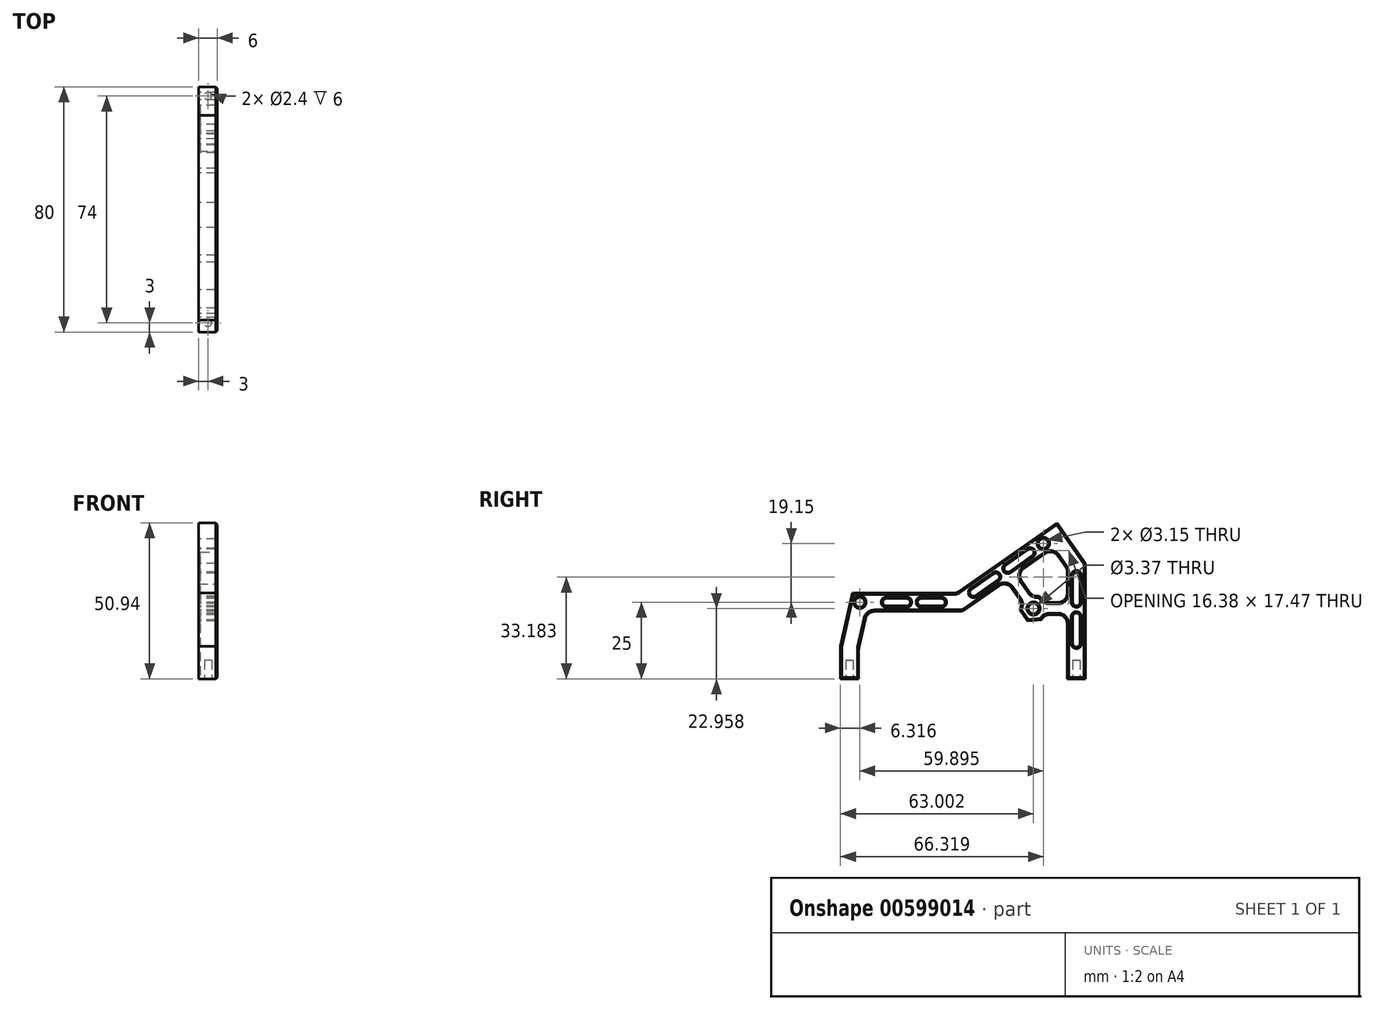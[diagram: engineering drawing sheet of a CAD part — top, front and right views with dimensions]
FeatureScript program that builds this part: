
annotation { "Feature Type Name" : "Feature", "Feature Type Description" : "" }
export const myFeature = defineFeature(function(context is Context, id is Id, definition is map)
    precondition{}
    {
        {
            var Q0;
            Q0=qCreatedBy(makeId("Top.planeOp"),FACE);
            var sketch = newSketch(context, id + "F0", { "sketchPlane" : qUnion([Q0])});
            skLineSegment(sketch, "E0", {"start": v(14, 40) * mm, "end": v(0, 40) * mm, "construction": true});
            skLineSegment(sketch, "E1", {"start": v(0, 40) * mm, "end": v(0, 0) * mm, "construction": true});
            skLineSegment(sketch, "E2", {"start": v(14, 40) * mm, "end": v(20, 40) * mm});
            skLineSegment(sketch, "E3", {"start": v(20, 40) * mm, "end": v(20, 0) * mm});
            skLineSegment(sketch, "E4", {"start": v(14, 40) * mm, "end": v(14, 0) * mm});
            skLineSegment(sketch, "E5.MirrorCS", {"start": v(14, -40) * mm, "end": v(20, -40) * mm});
            skLineSegment(sketch, "E6.MirrorCS", {"start": v(14, -40) * mm, "end": v(14, 0) * mm});
            skLineSegment(sketch, "E7.MirrorCS", {"start": v(20, -40) * mm, "end": v(20, 0) * mm});
            skLineSegment(sketch, "E8.MirrorCS", {"start": v(14, -40) * mm, "end": v(0, -40) * mm, "construction": true});
            skLineSegment(sketch, "E9.MirrorCS", {"start": v(0, -40) * mm, "end": v(0, 0) * mm, "construction": true});
            skLineSegment(sketch, "E10", {"start": v(14, 0) * mm, "end": v(29.88, 0) * mm, "construction": true});
            skLineSegment(sketch, "E11", {"start": v(20, 40) * mm, "end": v(20, 34) * mm, "construction": true});
            skPoint(sketch, "E12.centerSnap0", {"position": v(20, 37) * mm});
            skPoint(sketch, "E12.centerSnap1", {"position": v(17, 40) * mm});
            skSolve(sketch);
        }
        {
            var Q0;
            Q0=makeQuery(id+"F0.imprint","IMPRINT",FACE,{"disambiguationData":[TD([[makeQuery(id+"F0.imprint","IMPRINT",EDGE,{"derivedFrom":sQuery(id+"F0.wireOp",EDGE,"E2")}),-1.0]])]});
            extrude(context, id + "F1", {"entities" : qUnion([Q0]), "depth" : 70 * mm, "offsetDistance" : 25 * mm});
        }
        {
            var Q0;
            Q0=makeQuery(id+"F1.opExtrude","SWEPT_FACE",FACE,{"disambiguationData":[OSD([sQuery(id+"F0.wireOp",EDGE,"E4"),sQuery(id+"F0.wireOp",EDGE,"E6.MirrorCS")])]});
            var sketch = newSketch(context, id + "F2", { "sketchPlane" : qUnion([Q0])});
            skLineSegment(sketch, "E13", {"start": v(0, 0) * mm, "end": v(0, 28) * mm, "construction": true});
            skPoint(sketch, "E13.endSnap0", {"position": v(0, 0) * mm});
            skLineSegment(sketch, "E14", {"start": v(-20.33, 28) * mm, "end": v(19.67, 28) * mm, "construction": true});
            skLineSegment(sketch, "E15", {"start": v(2.08, 28) * mm, "end": v(-30.68, 50.94) * mm});
            skLineSegment(sketch, "E16", {"start": v(40, 10.6) * mm, "end": v(36.08, 28) * mm});
            skLineSegment(sketch, "E17", {"start": v(36.08, 28) * mm, "end": v(2.08, 28) * mm});
            skLineSegment(sketch, "E18", {"start": v(-30.68, 50.94) * mm, "end": v(-40, 37.64) * mm});
            skLineSegment(sketch, "E19", {"start": v(-40, 37.64) * mm, "end": v(-40, 0) * mm});
            skLineSegment(sketch, "E20", {"start": v(31.28, 22) * mm, "end": v(0.2, 22) * mm});
            skLineSegment(sketch, "E21", {"start": v(0.2, 22) * mm, "end": v(-14.18, 32.07) * mm});
            skLineSegment(sketch, "E22", {"start": v(-29.2, 42.59) * mm, "end": v(-34, 35.74) * mm});
            skLineSegment(sketch, "E23", {"start": v(-34, 35.74) * mm, "end": v(-34, 24.96) * mm});
            skLineSegment(sketch, "E24", {"start": v(-14.18, 32.07) * mm, "end": v(-21.96, 20.96) * mm});
            skLineSegment(sketch, "E25", {"start": v(-21.96, 20.96) * mm, "end": v(-34, 20.96) * mm});
            skLineSegment(sketch, "E26", {"start": v(-17.46, 34.36) * mm, "end": v(-24.04, 24.96) * mm});
            skLineSegment(sketch, "E27", {"start": v(-24.04, 24.96) * mm, "end": v(-34, 24.96) * mm});
            skLineSegment(sketch, "E28", {"start": v(-24.04, 24.96) * mm, "end": v(-21.96, 20.96) * mm, "construction": true});
            skCircle(sketch, "E29", {"center": v(-23, 22.96) * mm, "radius": 1.69 * mm});
            skLineSegment(sketch, "E30.trimOffspring", {"start": v(-17.46, 34.36) * mm, "end": v(-29.2, 42.59) * mm});
            skLineSegment(sketch, "E31.trimOffspring", {"start": v(-34, 20.96) * mm, "end": v(-34, 0) * mm});
            skLineSegment(sketch, "E32", {"start": v(-24.5, 46.6) * mm, "end": v(-26.21, 44.15) * mm, "construction": true});
            skCircle(sketch, "E33", {"center": v(-26.21, 44.15) * mm, "radius": 1.57 * mm});
            skLineSegment(sketch, "E34", {"start": v(36.08, 28) * mm, "end": v(31.28, 22) * mm, "construction": true});
            skCircle(sketch, "E35", {"center": v(33.68, 25) * mm, "radius": 1.57 * mm});
            skCircle(sketch, "E36.cCircle", {"center": v(-23, 22.96) * mm, "radius": 3.92 * mm, "construction": true});
            skLineSegment(sketch, "E36.0", {"start": v(-27.51, 23.35) * mm, "end": v(-24.92, 27.06) * mm});
            skLineSegment(sketch, "E36.1", {"start": v(-24.92, 27.06) * mm, "end": v(-20.4, 26.67) * mm});
            skLineSegment(sketch, "E36.2", {"start": v(-20.4, 26.67) * mm, "end": v(-18.5, 22.56) * mm});
            skLineSegment(sketch, "E36.3", {"start": v(-18.5, 22.56) * mm, "end": v(-21.09, 18.85) * mm});
            skLineSegment(sketch, "E36.4", {"start": v(-21.09, 18.85) * mm, "end": v(-25.6, 19.25) * mm});
            skLineSegment(sketch, "E36.5", {"start": v(-25.6, 19.25) * mm, "end": v(-27.51, 23.35) * mm});
            skPoint(sketch, "E36.0.midPoint", {"position": v(-26.21, 25.2) * mm});
            skLineSegment(sketch, "E37", {"start": v(-30.68, 50.94) * mm, "end": v(-30.68, 0) * mm, "construction": true});
            skLineSegment(sketch, "E38", {"start": v(-49.75, 0) * mm, "end": v(34, 0) * mm, "construction": true});
            skLineSegment(sketch, "E39", {"start": v(40, 10.6) * mm, "end": v(40, 0) * mm});
            skLineSegment(sketch, "E40", {"start": v(40, 0) * mm, "end": v(36.1, 0) * mm});
            skLineSegment(sketch, "E41", {"start": v(34, 9.92) * mm, "end": v(34, 0) * mm});
            skLineSegment(sketch, "E42.trimOffspring", {"start": v(42.25, 0) * mm, "end": v(49.74, 0) * mm, "construction": true});
            skLineSegment(sketch, "E43", {"start": v(40, 0) * mm, "end": v(34, 0) * mm});
            skLineSegment(sketch, "E44", {"start": v(31.28, 22) * mm, "end": v(34, 9.92) * mm});
            skLineSegment(sketch, "E45", {"start": v(0.2, 22) * mm, "end": v(31.28, 22) * mm});
            skLineSegment(sketch, "E46", {"start": v(40, 0) * mm, "end": v(40, 10.6) * mm});
            skLineSegment(sketch, "E47", {"start": v(7.02, 26.2) * mm, "end": v(13.64, 26.2) * mm});
            skLineSegment(sketch, "E48", {"start": v(2.08, 28) * mm, "end": v(2.08, 22) * mm, "construction": true});
            skLineSegment(sketch, "E49", {"start": v(7.02, 23.8) * mm, "end": v(7.02, 26.2) * mm, "construction": true});
            skLineSegment(sketch, "E50", {"start": v(25.02, 23.8) * mm, "end": v(25.02, 26.2) * mm, "construction": true});
            skCircle(sketch, "E51", {"center": v(7.02, 25) * mm, "radius": 1.2 * mm});
            skCircle(sketch, "E52", {"center": v(25.02, 25) * mm, "radius": 1.2 * mm});
            skLineSegment(sketch, "E53", {"start": v(-35.8, 33.72) * mm, "end": v(-35.8, 25.03) * mm});
            skLineSegment(sketch, "E54", {"start": v(-38.2, 33.72) * mm, "end": v(-38.2, 25.03) * mm});
            skLineSegment(sketch, "E55", {"start": v(-35.8, 33.72) * mm, "end": v(-38.2, 33.72) * mm, "construction": true});
            skLineSegment(sketch, "E56", {"start": v(-35.8, 11.57) * mm, "end": v(-38.2, 11.57) * mm, "construction": true});
            skCircle(sketch, "E57", {"center": v(-37, 33.72) * mm, "radius": 1.2 * mm});
            skCircle(sketch, "E58", {"center": v(-37, 11.57) * mm, "radius": 1.2 * mm});
            skLineSegment(sketch, "E59", {"start": v(-22.6, 40.16) * mm, "end": v(-15.28, 35.04) * mm});
            skLineSegment(sketch, "E60", {"start": v(-22.6, 40.16) * mm, "end": v(-21.23, 42.11) * mm, "construction": true});
            skLineSegment(sketch, "E61", {"start": v(-21.23, 42.11) * mm, "end": v(-13.92, 37) * mm});
            skLineSegment(sketch, "E62", {"start": v(-2.7, 29.14) * mm, "end": v(-4.07, 27.2) * mm, "construction": true});
            skCircle(sketch, "E63", {"center": v(-21.9, 41.14) * mm, "radius": 1.2 * mm});
            skCircle(sketch, "E64", {"center": v(-3.39, 28.17) * mm, "radius": 1.2 * mm});
            skLineSegment(sketch, "E65", {"start": v(5.46, 28) * mm, "end": v(5.46, 22) * mm, "construction": true});
            skLineSegment(sketch, "E66", {"start": v(5.46, 25) * mm, "end": v(7.02, 25) * mm, "construction": true});
            skLineSegment(sketch, "E67", {"start": v(-22.05, 44.9) * mm, "end": v(-25.5, 39.98) * mm, "construction": true});
            skLineSegment(sketch, "E68", {"start": v(-23.77, 42.44) * mm, "end": v(-21.9, 41.14) * mm, "construction": true});
            skLineSegment(sketch, "E69", {"start": v(-34, 35.47) * mm, "end": v(-40, 35.47) * mm, "construction": true});
            skLineSegment(sketch, "E70", {"start": v(-37, 35.47) * mm, "end": v(-37, 33.72) * mm, "construction": true});
            skLineSegment(sketch, "E71", {"start": v(16.02, 26.2) * mm, "end": v(16.02, 23.8) * mm, "construction": true});
            skLineSegment(sketch, "E72", {"start": v(-35.8, 22.65) * mm, "end": v(-38.2, 22.65) * mm, "construction": true});
            skLineSegment(sketch, "E73", {"start": v(-12.65, 34.65) * mm, "end": v(-21.9, 41.14) * mm, "construction": true});
            skLineSegment(sketch, "E74", {"start": v(-12.65, 34.65) * mm, "end": v(-3.39, 28.17) * mm, "construction": true});
            skLineSegment(sketch, "E75", {"start": v(25.02, 25) * mm, "end": v(7.02, 25) * mm, "construction": true});
            skCircle(sketch, "E76", {"center": v(13.64, 25) * mm, "radius": 1.2 * mm});
            skCircle(sketch, "E77", {"center": v(18.4, 25) * mm, "radius": 1.2 * mm});
            skCircle(sketch, "E78", {"center": v(-10.7, 33.29) * mm, "radius": 1.2 * mm});
            skCircle(sketch, "E79", {"center": v(-14.6, 36.02) * mm, "radius": 1.2 * mm});
            skLineSegment(sketch, "E80", {"start": v(-37, 33.72) * mm, "end": v(-37, 11.57) * mm, "construction": true});
            skCircle(sketch, "E81", {"center": v(-37, 25.03) * mm, "radius": 1.2 * mm});
            skCircle(sketch, "E82", {"center": v(-37, 20.27) * mm, "radius": 1.2 * mm});
            skLineSegment(sketch, "E83.trimOffspring", {"start": v(-11.38, 32.31) * mm, "end": v(-4.07, 27.2) * mm});
            skPoint(sketch, "E84.orphan", {"position": v(-13.33, 33.68) * mm});
            skPoint(sketch, "E85.start.orphan", {"position": v(-11.96, 35.63) * mm});
            skLineSegment(sketch, "E86.trimOffspring", {"start": v(-10.01, 34.26) * mm, "end": v(-2.7, 29.14) * mm});
            skLineSegment(sketch, "E87.trimOffspring", {"start": v(18.4, 23.8) * mm, "end": v(25.02, 23.8) * mm});
            skLineSegment(sketch, "E88.trimOffspring", {"start": v(18.4, 26.2) * mm, "end": v(25.02, 26.2) * mm});
            skLineSegment(sketch, "E89", {"start": v(7.02, 23.8) * mm, "end": v(13.64, 23.8) * mm});
            skLineSegment(sketch, "E90.trimOffspring", {"start": v(-35.8, 20.27) * mm, "end": v(-35.8, 11.57) * mm});
            skLineSegment(sketch, "E91.trimOffspring", {"start": v(-38.2, 20.27) * mm, "end": v(-38.2, 11.57) * mm});
            skSolve(sketch);
        }
        {
            var Q0;
            {var subQ1=sQuery(id+"F2.wireOp",EDGE,"E21");Q0=makeQuery(id+"F2.imprint","IMPRINT",FACE,{"disambiguationData":[TD([[makeQuery(id+"F2.imprint","IMPRINT",EDGE,{"derivedFrom":subQ1}),1.0]])]});}
            var Q1;
            Q1=makeQuery(id+"F2.imprint","IMPRINT",FACE,{"disambiguationData":[TD([[makeQuery(id+"F2.imprint","IMPRINT",EDGE,{"derivedFrom":sQuery(id+"F2.wireOp",EDGE,"E22")}),1.0]])]});
            var Q2;
            Q2=makeQuery(id+"F2.imprint","IMPRINT",FACE,{"disambiguationData":[TD([[makeQuery(id+"F2.imprint","IMPRINT",EDGE,{"derivedFrom":sQuery(id+"F2.wireOp",EDGE,"E15")}),-1.0]])]});
            var Q3;
            Q3=makeQuery(id+"F2.imprint","IMPRINT",FACE,{"disambiguationData":[TD([[makeQuery(id+"F2.imprint","IMPRINT",EDGE,{"derivedFrom":sQuery(id+"F2.wireOp",EDGE,"E33")}),1.0]])]});
            var Q4;
            Q4=makeQuery(id+"F2.imprint","IMPRINT",FACE,{"disambiguationData":[TD([[makeQuery(id+"F2.imprint","IMPRINT",EDGE,{"derivedFrom":sQuery(id+"F2.wireOp",EDGE,"E29")}),1.0]])]});
            var Q5;
            Q5=makeQuery(id+"F2.imprint","IMPRINT",FACE,{"disambiguationData":[TD([[makeQuery(id+"F2.imprint","IMPRINT",EDGE,{"derivedFrom":sQuery(id+"F2.wireOp",EDGE,"E35")}),1.0]])]});
            var Q6;
            {var subQ0=sQuery(id+"F2.wireOp",EDGE,"E51");var subQ1=makeQuery(id+"F2.imprint","INTERSECT",VERTEX,{"derivedFrom":[sQuery(id+"F2.wireOp",EDGE,"E47"),subQ0]});Q6=makeQuery(id+"F2.imprint","IMPRINT",FACE,{"disambiguationData":[TD([[makeQuery(id+"F2.imprint","IMPRINT",EDGE,{"disambiguationData":[TD([[subQ1,-1.0]])],"derivedFrom":subQ0}),1.0]])]});}
            var Q7;
            {var subQ0=sQuery(id+"F2.wireOp",EDGE,"E52");var subQ1=makeQuery(id+"F2.imprint","INTERSECT",VERTEX,{"derivedFrom":[sQuery(id+"F2.wireOp",EDGE,"E47"),subQ0]});Q7=makeQuery(id+"F2.imprint","IMPRINT",FACE,{"disambiguationData":[TD([[makeQuery(id+"F2.imprint","IMPRINT",EDGE,{"disambiguationData":[TD([[subQ1,-1.0]])],"derivedFrom":subQ0}),1.0]])]});}
            var Q8;
            {var subQ0=sQuery(id+"F2.wireOp",EDGE,"E57");var subQ1=makeQuery(id+"F2.imprint","INTERSECT",VERTEX,{"derivedFrom":[sQuery(id+"F2.wireOp",EDGE,"E53"),subQ0]});Q8=makeQuery(id+"F2.imprint","IMPRINT",FACE,{"disambiguationData":[TD([[makeQuery(id+"F2.imprint","IMPRINT",EDGE,{"disambiguationData":[TD([[subQ1,-1.0]])],"derivedFrom":subQ0}),1.0]])]});}
            var Q9;
            {var subQ0=sQuery(id+"F2.wireOp",EDGE,"E58");var subQ1=makeQuery(id+"F2.imprint","INTERSECT",VERTEX,{"derivedFrom":[sQuery(id+"F2.wireOp",EDGE,"E53"),subQ0]});Q9=makeQuery(id+"F2.imprint","IMPRINT",FACE,{"disambiguationData":[TD([[makeQuery(id+"F2.imprint","IMPRINT",EDGE,{"disambiguationData":[TD([[subQ1,-1.0]])],"derivedFrom":subQ0}),1.0]])]});}
            var Q10;
            {var subQ0=sQuery(id+"F2.wireOp",EDGE,"E63");var subQ1=makeQuery(id+"F2.imprint","INTERSECT",VERTEX,{"derivedFrom":[sQuery(id+"F2.wireOp",EDGE,"E59"),subQ0]});Q10=makeQuery(id+"F2.imprint","IMPRINT",FACE,{"disambiguationData":[TD([[makeQuery(id+"F2.imprint","IMPRINT",EDGE,{"disambiguationData":[TD([[subQ1,1.0]])],"derivedFrom":subQ0}),1.0]])]});}
            var Q11;
            {var subQ0=sQuery(id+"F2.wireOp",EDGE,"E64");var subQ1=makeQuery(id+"F2.imprint","INTERSECT",VERTEX,{"derivedFrom":[sQuery(id+"F2.wireOp",EDGE,"E59"),subQ0]});Q11=makeQuery(id+"F2.imprint","IMPRINT",FACE,{"disambiguationData":[TD([[makeQuery(id+"F2.imprint","IMPRINT",EDGE,{"disambiguationData":[TD([[subQ1,1.0]])],"derivedFrom":subQ0}),1.0]])]});}
            var Q12;
            {var subQ0=sQuery(id+"F2.wireOp",EDGE,"E58");var subQ1=sQuery(id+"F2.wireOp",EDGE,"E53");var subQ2=makeQuery(id+"F2.imprint","INTERSECT",VERTEX,{"derivedFrom":[subQ1,subQ0]});Q12=makeQuery(id+"F2.imprint","IMPRINT",FACE,{"disambiguationData":[TD([[makeQuery(id+"F2.imprint","IMPRINT",EDGE,{"disambiguationData":[TD([[subQ2,1.0]])],"derivedFrom":subQ1}),-1.0]])]});}
            var Q13;
            {var subQ0=sQuery(id+"F2.wireOp",EDGE,"E82");var subQ1=sQuery(id+"F2.wireOp",EDGE,"EsRLWaQp-72Lr-nXQH-179a-LBt1Ee8kWsKf");var subQ2=makeQuery(id+"F2.imprint","INTERSECT",VERTEX,{"disambiguationData":[OD(0.0)],"derivedFrom":[subQ1,subQ0]});Q13=makeQuery(id+"F2.imprint","IMPRINT",FACE,{"disambiguationData":[TD([[makeQuery(id+"F2.imprint","IMPRINT",EDGE,{"disambiguationData":[TD([[subQ2,-1.0]])],"derivedFrom":subQ1}),-1.0]])]});}
            var Q14;
            {var subQ0=sQuery(id+"F2.wireOp",EDGE,"E82");var subQ1=sQuery(id+"F2.wireOp",EDGE,"EsRLWaQp-72Lr-nXQH-179a-LBt1Ee8kWsKf");var subQ2=makeQuery(id+"F2.imprint","INTERSECT",VERTEX,{"disambiguationData":[OD(0.0)],"derivedFrom":[subQ1,subQ0]});Q14=makeQuery(id+"F2.imprint","IMPRINT",FACE,{"disambiguationData":[TD([[makeQuery(id+"F2.imprint","IMPRINT",EDGE,{"disambiguationData":[TD([[subQ2,-1.0]])],"derivedFrom":subQ1}),1.0]])]});}
            var Q15;
            {var subQ0=sQuery(id+"F2.wireOp",EDGE,"E57");var subQ1=sQuery(id+"F2.wireOp",EDGE,"E53");var subQ2=makeQuery(id+"F2.imprint","INTERSECT",VERTEX,{"derivedFrom":[subQ1,subQ0]});Q15=makeQuery(id+"F2.imprint","IMPRINT",FACE,{"disambiguationData":[TD([[makeQuery(id+"F2.imprint","IMPRINT",EDGE,{"disambiguationData":[TD([[subQ2,-1.0]])],"derivedFrom":subQ1}),-1.0]])]});}
            var Q16;
            {var subQ0=sQuery(id+"F2.wireOp",EDGE,"E81");var subQ1=sQuery(id+"F2.wireOp",EDGE,"dPTXOL7o-P8y6-gZZ0-hFhJ-cb4R31KIsnZc");var subQ2=makeQuery(id+"F2.imprint","INTERSECT",VERTEX,{"disambiguationData":[OD(0.0)],"derivedFrom":[subQ1,subQ0]});Q16=makeQuery(id+"F2.imprint","IMPRINT",FACE,{"disambiguationData":[TD([[makeQuery(id+"F2.imprint","IMPRINT",EDGE,{"disambiguationData":[TD([[subQ2,-1.0]])],"derivedFrom":subQ1}),-1.0]])]});}
            var Q17;
            {var subQ0=sQuery(id+"F2.wireOp",EDGE,"E81");var subQ1=sQuery(id+"F2.wireOp",EDGE,"dPTXOL7o-P8y6-gZZ0-hFhJ-cb4R31KIsnZc");var subQ2=makeQuery(id+"F2.imprint","INTERSECT",VERTEX,{"disambiguationData":[OD(0.0)],"derivedFrom":[subQ1,subQ0]});Q17=makeQuery(id+"F2.imprint","IMPRINT",FACE,{"disambiguationData":[TD([[makeQuery(id+"F2.imprint","IMPRINT",EDGE,{"disambiguationData":[TD([[subQ2,-1.0]])],"derivedFrom":subQ1}),1.0]])]});}
            var Q18;
            {var subQ0=sQuery(id+"F2.wireOp",EDGE,"E63");var subQ1=sQuery(id+"F2.wireOp",EDGE,"E59");var subQ2=makeQuery(id+"F2.imprint","INTERSECT",VERTEX,{"derivedFrom":[subQ1,subQ0]});Q18=makeQuery(id+"F2.imprint","IMPRINT",FACE,{"disambiguationData":[TD([[makeQuery(id+"F2.imprint","IMPRINT",EDGE,{"disambiguationData":[TD([[subQ2,-1.0]])],"derivedFrom":subQ1}),1.0]])]});}
            var Q19;
            {var subQ0=sQuery(id+"F2.wireOp",EDGE,"E79");var subQ1=sQuery(id+"F2.wireOp",EDGE,"iujlU8PM-xRd4-Xfqd-nS0c-G3hk0IdFOhpx");var subQ2=makeQuery(id+"F2.imprint","INTERSECT",VERTEX,{"disambiguationData":[OD(0.0)],"derivedFrom":[subQ1,subQ0]});Q19=makeQuery(id+"F2.imprint","IMPRINT",FACE,{"disambiguationData":[TD([[makeQuery(id+"F2.imprint","IMPRINT",EDGE,{"disambiguationData":[TD([[subQ2,-1.0]])],"derivedFrom":subQ1}),-1.0]])]});}
            var Q20;
            {var subQ0=sQuery(id+"F2.wireOp",EDGE,"E79");var subQ1=sQuery(id+"F2.wireOp",EDGE,"iujlU8PM-xRd4-Xfqd-nS0c-G3hk0IdFOhpx");var subQ2=makeQuery(id+"F2.imprint","INTERSECT",VERTEX,{"disambiguationData":[OD(0.0)],"derivedFrom":[subQ1,subQ0]});Q20=makeQuery(id+"F2.imprint","IMPRINT",FACE,{"disambiguationData":[TD([[makeQuery(id+"F2.imprint","IMPRINT",EDGE,{"disambiguationData":[TD([[subQ2,-1.0]])],"derivedFrom":subQ1}),1.0]])]});}
            var Q21;
            {var subQ0=sQuery(id+"F2.wireOp",EDGE,"E64");var subQ1=sQuery(id+"F2.wireOp",EDGE,"E59");var subQ2=makeQuery(id+"F2.imprint","INTERSECT",VERTEX,{"derivedFrom":[subQ1,subQ0]});Q21=makeQuery(id+"F2.imprint","IMPRINT",FACE,{"disambiguationData":[TD([[makeQuery(id+"F2.imprint","IMPRINT",EDGE,{"disambiguationData":[TD([[subQ2,1.0]])],"derivedFrom":subQ1}),1.0]])]});}
            var Q22;
            {var subQ0=sQuery(id+"F2.wireOp",EDGE,"E78");var subQ1=sQuery(id+"F2.wireOp",EDGE,"WhBVlu8J-ggpT-rPkh-PH5j-TZSZnhHrwUjz");var subQ2=makeQuery(id+"F2.imprint","INTERSECT",VERTEX,{"disambiguationData":[OD(0.0)],"derivedFrom":[subQ1,subQ0]});Q22=makeQuery(id+"F2.imprint","IMPRINT",FACE,{"disambiguationData":[TD([[makeQuery(id+"F2.imprint","IMPRINT",EDGE,{"disambiguationData":[TD([[subQ2,1.0]])],"derivedFrom":subQ1}),-1.0]])]});}
            var Q23;
            {var subQ0=sQuery(id+"F2.wireOp",EDGE,"E78");var subQ1=sQuery(id+"F2.wireOp",EDGE,"WhBVlu8J-ggpT-rPkh-PH5j-TZSZnhHrwUjz");var subQ2=makeQuery(id+"F2.imprint","INTERSECT",VERTEX,{"disambiguationData":[OD(0.0)],"derivedFrom":[subQ1,subQ0]});Q23=makeQuery(id+"F2.imprint","IMPRINT",FACE,{"disambiguationData":[TD([[makeQuery(id+"F2.imprint","IMPRINT",EDGE,{"disambiguationData":[TD([[subQ2,1.0]])],"derivedFrom":subQ1}),1.0]])]});}
            var Q24;
            {var subQ0=sQuery(id+"F2.wireOp",EDGE,"E51");var subQ1=sQuery(id+"F2.wireOp",EDGE,"E47");var subQ2=makeQuery(id+"F2.imprint","INTERSECT",VERTEX,{"derivedFrom":[subQ1,subQ0]});Q24=makeQuery(id+"F2.imprint","IMPRINT",FACE,{"disambiguationData":[TD([[makeQuery(id+"F2.imprint","IMPRINT",EDGE,{"disambiguationData":[TD([[subQ2,-1.0]])],"derivedFrom":subQ1}),-1.0]])]});}
            var Q25;
            {var subQ0=sQuery(id+"F2.wireOp",EDGE,"E76");var subQ1=sQuery(id+"F2.wireOp",EDGE,"A0GBhmAl-cezT-vBN6-2keo-XJEfcKbMd6cT");var subQ2=makeQuery(id+"F2.imprint","INTERSECT",VERTEX,{"disambiguationData":[OD(0.0)],"derivedFrom":[subQ1,subQ0]});Q25=makeQuery(id+"F2.imprint","IMPRINT",FACE,{"disambiguationData":[TD([[makeQuery(id+"F2.imprint","IMPRINT",EDGE,{"disambiguationData":[TD([[subQ2,-1.0]])],"derivedFrom":subQ1}),-1.0]])]});}
            var Q26;
            {var subQ0=sQuery(id+"F2.wireOp",EDGE,"E76");var subQ1=sQuery(id+"F2.wireOp",EDGE,"A0GBhmAl-cezT-vBN6-2keo-XJEfcKbMd6cT");var subQ2=makeQuery(id+"F2.imprint","INTERSECT",VERTEX,{"disambiguationData":[OD(0.0)],"derivedFrom":[subQ1,subQ0]});Q26=makeQuery(id+"F2.imprint","IMPRINT",FACE,{"disambiguationData":[TD([[makeQuery(id+"F2.imprint","IMPRINT",EDGE,{"disambiguationData":[TD([[subQ2,-1.0]])],"derivedFrom":subQ1}),1.0]])]});}
            var Q27;
            {var subQ0=sQuery(id+"F2.wireOp",EDGE,"E52");var subQ1=sQuery(id+"F2.wireOp",EDGE,"E47");var subQ2=makeQuery(id+"F2.imprint","INTERSECT",VERTEX,{"derivedFrom":[subQ1,subQ0]});Q27=makeQuery(id+"F2.imprint","IMPRINT",FACE,{"disambiguationData":[TD([[makeQuery(id+"F2.imprint","IMPRINT",EDGE,{"disambiguationData":[TD([[subQ2,1.0]])],"derivedFrom":subQ1}),-1.0]])]});}
            var Q28;
            {var subQ0=sQuery(id+"F2.wireOp",EDGE,"E77");var subQ1=sQuery(id+"F2.wireOp",EDGE,"UBjIhsa9-i5sD-a0D1-aE2p-8xy051tw6F00");var subQ2=makeQuery(id+"F2.imprint","INTERSECT",VERTEX,{"disambiguationData":[OD(0.0)],"derivedFrom":[subQ1,subQ0]});Q28=makeQuery(id+"F2.imprint","IMPRINT",FACE,{"disambiguationData":[TD([[makeQuery(id+"F2.imprint","IMPRINT",EDGE,{"disambiguationData":[TD([[subQ2,1.0]])],"derivedFrom":subQ1}),-1.0]])]});}
            var Q29;
            {var subQ0=sQuery(id+"F2.wireOp",EDGE,"E77");var subQ1=sQuery(id+"F2.wireOp",EDGE,"UBjIhsa9-i5sD-a0D1-aE2p-8xy051tw6F00");var subQ2=makeQuery(id+"F2.imprint","INTERSECT",VERTEX,{"disambiguationData":[OD(0.0)],"derivedFrom":[subQ1,subQ0]});Q29=makeQuery(id+"F2.imprint","IMPRINT",FACE,{"disambiguationData":[TD([[makeQuery(id+"F2.imprint","IMPRINT",EDGE,{"disambiguationData":[TD([[subQ2,1.0]])],"derivedFrom":subQ1}),1.0]])]});}
            var Q30;
            {var subQ0=sQuery(id+"F2.wireOp",EDGE,"E90.trimOffspring");Q30=makeQuery(id+"F2.imprint","IMPRINT",FACE,{"disambiguationData":[TD([[makeQuery(id+"F2.imprint","IMPRINT",EDGE,{"derivedFrom":subQ0}),-1.0]])]});}
            var Q31;
            {var subQ0=sQuery(id+"F2.wireOp",EDGE,"E82");var subQ1=makeQuery(id+"F2.imprint","INTERSECT",VERTEX,{"derivedFrom":[subQ0,sQuery(id+"F2.wireOp",EDGE,"E90.trimOffspring")]});Q31=makeQuery(id+"F2.imprint","IMPRINT",FACE,{"disambiguationData":[TD([[makeQuery(id+"F2.imprint","IMPRINT",EDGE,{"disambiguationData":[TD([[subQ1,-1.0]])],"derivedFrom":subQ0}),1.0]])]});}
            var Q32;
            {var subQ0=sQuery(id+"F2.wireOp",EDGE,"E81");var subQ1=makeQuery(id+"F2.imprint","INTERSECT",VERTEX,{"derivedFrom":[sQuery(id+"F2.wireOp",EDGE,"E53"),subQ0]});Q32=makeQuery(id+"F2.imprint","IMPRINT",FACE,{"disambiguationData":[TD([[makeQuery(id+"F2.imprint","IMPRINT",EDGE,{"disambiguationData":[TD([[subQ1,-1.0]])],"derivedFrom":subQ0}),1.0]])]});}
            var Q33;
            {var subQ0=sQuery(id+"F2.wireOp",EDGE,"E79");var subQ1=makeQuery(id+"F2.imprint","INTERSECT",VERTEX,{"derivedFrom":[sQuery(id+"F2.wireOp",EDGE,"E59"),subQ0]});Q33=makeQuery(id+"F2.imprint","IMPRINT",FACE,{"disambiguationData":[TD([[makeQuery(id+"F2.imprint","IMPRINT",EDGE,{"disambiguationData":[TD([[subQ1,1.0]])],"derivedFrom":subQ0}),1.0]])]});}
            var Q34;
            {var subQ0=sQuery(id+"F2.wireOp",EDGE,"E78");var subQ1=makeQuery(id+"F2.imprint","INTERSECT",VERTEX,{"derivedFrom":[subQ0,sQuery(id+"F2.wireOp",EDGE,"E83.trimOffspring")]});Q34=makeQuery(id+"F2.imprint","IMPRINT",FACE,{"disambiguationData":[TD([[makeQuery(id+"F2.imprint","IMPRINT",EDGE,{"disambiguationData":[TD([[subQ1,1.0]])],"derivedFrom":subQ0}),1.0]])]});}
            var Q35;
            {var subQ0=sQuery(id+"F2.wireOp",EDGE,"E83.trimOffspring");Q35=makeQuery(id+"F2.imprint","IMPRINT",FACE,{"disambiguationData":[TD([[makeQuery(id+"F2.imprint","IMPRINT",EDGE,{"derivedFrom":subQ0}),1.0]])]});}
            var Q36;
            {var subQ0=sQuery(id+"F2.wireOp",EDGE,"E76");var subQ1=makeQuery(id+"F2.imprint","INTERSECT",VERTEX,{"derivedFrom":[sQuery(id+"F2.wireOp",EDGE,"E47"),subQ0]});Q36=makeQuery(id+"F2.imprint","IMPRINT",FACE,{"disambiguationData":[TD([[makeQuery(id+"F2.imprint","IMPRINT",EDGE,{"disambiguationData":[TD([[subQ1,-1.0]])],"derivedFrom":subQ0}),1.0]])]});}
            var Q37;
            {var subQ0=sQuery(id+"F2.wireOp",EDGE,"E77");var subQ1=makeQuery(id+"F2.imprint","INTERSECT",VERTEX,{"derivedFrom":[subQ0,sQuery(id+"F2.wireOp",EDGE,"E87.trimOffspring")]});Q37=makeQuery(id+"F2.imprint","IMPRINT",FACE,{"disambiguationData":[TD([[makeQuery(id+"F2.imprint","IMPRINT",EDGE,{"disambiguationData":[TD([[subQ1,1.0]])],"derivedFrom":subQ0}),1.0]])]});}
            var Q38;
            {var subQ0=sQuery(id+"F2.wireOp",EDGE,"E87.trimOffspring");Q38=makeQuery(id+"F2.imprint","IMPRINT",FACE,{"disambiguationData":[TD([[makeQuery(id+"F2.imprint","IMPRINT",EDGE,{"derivedFrom":subQ0}),1.0]])]});}
            extrude(context, id + "F3", {"entities" : qUnion([Q0, Q1, Q2, Q3, Q4, Q5, Q6, Q7, Q8, Q9, Q10, Q11, Q12, Q13, Q14, Q15, Q16, Q17, Q18, Q19, Q20, Q21, Q22, Q23, Q24, Q25, Q26, Q27, Q28, Q29, Q30, Q31, Q32, Q33, Q34, Q35, Q36, Q37, Q38]), "operationType" : NewBodyOperationType.REMOVE, "oppositeDirection" : true, "depth" : 25 * mm, "offsetDistance" : 25 * mm});
        }
        {
            var Q0;
            Q0=makeQuery(id+"F0.imprint","IMPRINT",FACE,{"disambiguationData":[TD([[makeQuery(id+"F0.imprint","IMPRINT",EDGE,{"derivedFrom":sQuery(id+"F0.wireOp",EDGE,"E2")}),-1.0]])]});
            var sketch = newSketch(context, id + "F4", { "sketchPlane" : qUnion([Q0])});
            skLineSegment(sketch, "E92", {"start": v(0, 0) * mm, "end": v(0, 40) * mm, "construction": true});
            skLineSegment(sketch, "E93", {"start": v(0, 40) * mm, "end": v(14, 40) * mm, "construction": true});
            skLineSegment(sketch, "E94", {"start": v(14, 40) * mm, "end": v(20, 40) * mm, "construction": true});
            skLineSegment(sketch, "E95", {"start": v(20, 40) * mm, "end": v(20, 34) * mm, "construction": true});
            skLineSegment(sketch, "E96", {"start": v(20, 34) * mm, "end": v(14, 34) * mm, "construction": true});
            skLineSegment(sketch, "E97", {"start": v(14, 34) * mm, "end": v(14, 40) * mm, "construction": true});
            skCircle(sketch, "E98", {"center": v(17, 37) * mm, "radius": 1.2 * mm});
            skPoint(sketch, "E98.centerSnap0", {"position": v(20, 37) * mm});
            skPoint(sketch, "E98.centerSnap1", {"position": v(17, 34) * mm});
            skLineSegment(sketch, "E99", {"start": v(0, 0) * mm, "end": v(0, -40) * mm, "construction": true});
            skLineSegment(sketch, "E100", {"start": v(0, -40) * mm, "end": v(14, -40) * mm, "construction": true});
            skLineSegment(sketch, "E101", {"start": v(14, -40) * mm, "end": v(20, -40) * mm, "construction": true});
            skLineSegment(sketch, "E102", {"start": v(20, -40) * mm, "end": v(20, -34) * mm, "construction": true});
            skLineSegment(sketch, "E103", {"start": v(20, -34) * mm, "end": v(14, -34) * mm, "construction": true});
            skLineSegment(sketch, "E104", {"start": v(14, -34) * mm, "end": v(14, -40) * mm, "construction": true});
            skCircle(sketch, "E105", {"center": v(17, -37) * mm, "radius": 1.2 * mm});
            skPoint(sketch, "E105.centerSnap0", {"position": v(17, -40) * mm});
            skPoint(sketch, "E105.centerSnap1", {"position": v(20, -37) * mm});
            skSolve(sketch);
        }
        {
            var Q0;
            Q0 = qSketchRegion(id + "F4", true);
            extrude(context, id + "F5", {"entities" : qUnion([Q0]), "operationType" : NewBodyOperationType.REMOVE, "depth" : 6 * mm, "offsetDistance" : 25 * mm});
        }
        {
            var Q0;
            Q0=makeQuery(id+"F3.boolean.opBoolean","COPY",EDGE,{"derivedFrom":makeQuery(id+"F3.opExtrude","SWEPT_EDGE",EDGE,{"disambiguationData":[OSD([sQuery(id+"F2.wireOp",EDGE,"E26"),sQuery(id+"F2.wireOp",EDGE,"E36.1")])]})});
            var Q1;
            Q1=makeQuery(id+"F3.boolean.opBoolean","COPY",EDGE,{"derivedFrom":makeQuery(id+"F3.opExtrude","SWEPT_EDGE",EDGE,{"disambiguationData":[OSD([sQuery(id+"F2.wireOp",EDGE,"E27"),sQuery(id+"F2.wireOp",EDGE,"E36.0")])]})});
            var Q2;
            Q2=makeQuery(id+"F3.boolean.opBoolean","COPY",EDGE,{"derivedFrom":makeQuery(id+"F3.opExtrude","SWEPT_EDGE",EDGE,{"disambiguationData":[OSD([sQuery(id+"F2.wireOp",EDGE,"E23"),sQuery(id+"F2.wireOp",EDGE,"E27")])]})});
            var Q3;
            Q3=makeQuery(id+"F3.boolean.opBoolean","COPY",EDGE,{"derivedFrom":makeQuery(id+"F3.opExtrude","SWEPT_EDGE",EDGE,{"disambiguationData":[OSD([sQuery(id+"F2.wireOp",EDGE,"E22"),sQuery(id+"F2.wireOp",EDGE,"E23")])]})});
            var Q4;
            Q4=makeQuery(id+"F3.boolean.opBoolean","COPY",EDGE,{"derivedFrom":makeQuery(id+"F3.opExtrude","SWEPT_EDGE",EDGE,{"disambiguationData":[OSD([sQuery(id+"F2.wireOp",EDGE,"E22"),sQuery(id+"F2.wireOp",EDGE,"E30.trimOffspring")])]})});
            var Q5;
            Q5=makeQuery(id+"F3.boolean.opBoolean","COPY",EDGE,{"derivedFrom":makeQuery(id+"F3.opExtrude","SWEPT_EDGE",EDGE,{"disambiguationData":[OSD([sQuery(id+"F2.wireOp",EDGE,"E26"),sQuery(id+"F2.wireOp",EDGE,"E30.trimOffspring")])]})});
            var Q6;
            Q6=makeQuery(id+"F3.boolean.opBoolean","COPY",EDGE,{"derivedFrom":makeQuery(id+"F3.opExtrude","SWEPT_EDGE",EDGE,{"disambiguationData":[OSD([sQuery(id+"F2.wireOp",EDGE,"E21"),sQuery(id+"F2.wireOp",EDGE,"E24")])]})});
            var Q7;
            Q7=makeQuery(id+"F3.boolean.opBoolean","COPY",EDGE,{"derivedFrom":makeQuery(id+"F3.opExtrude","SWEPT_EDGE",EDGE,{"disambiguationData":[OSD([sQuery(id+"F2.wireOp",EDGE,"E24"),sQuery(id+"F2.wireOp",EDGE,"E36.2")])]})});
            var Q8;
            Q8=makeQuery(id+"F3.boolean.opBoolean","COPY",EDGE,{"derivedFrom":makeQuery(id+"F3.opExtrude","SWEPT_EDGE",EDGE,{"disambiguationData":[OSD([sQuery(id+"F2.wireOp",EDGE,"E25"),sQuery(id+"F2.wireOp",EDGE,"E36.5")])]})});
            var Q9;
            Q9=makeQuery(id+"F3.boolean.opBoolean","COPY",EDGE,{"derivedFrom":makeQuery(id+"F3.opExtrude","SWEPT_EDGE",EDGE,{"disambiguationData":[OSD([sQuery(id+"F2.wireOp",EDGE,"E25"),sQuery(id+"F2.wireOp",EDGE,"E31.trimOffspring")])]})});
            var Q10;
            Q10=makeQuery(id+"F3.boolean.opBoolean","COPY",EDGE,{"derivedFrom":makeQuery(id+"F3.opExtrude","SWEPT_EDGE",EDGE,{"disambiguationData":[OSD([sQuery(id+"F2.wireOp",EDGE,"E44"),sQuery(id+"F2.wireOp",EDGE,"E45")])]})});
            var Q11;
            Q11=makeQuery(id+"F3.boolean.opBoolean","COPY",EDGE,{"derivedFrom":makeQuery(id+"F3.opExtrude","SWEPT_EDGE",EDGE,{"disambiguationData":[OSD([sQuery(id+"F2.wireOp",EDGE,"E44"),sQuery(id+"F2.wireOp",EDGE,"E41")])]})});
            var Q12;
            Q12=makeQuery(id+"F3.boolean.opBoolean","COPY",EDGE,{"derivedFrom":makeQuery(id+"F3.opExtrude","SWEPT_EDGE",EDGE,{"disambiguationData":[OSD([sQuery(id+"F0.wireOp",EDGE,"E2"),sQuery(id+"F0.wireOp",EDGE,"E4"),sQuery(id+"F2.wireOp",EDGE,"E18"),sQuery(id+"F2.wireOp",EDGE,"E19")])]})});
            var Q13;
            Q13=makeQuery(id+"F3.boolean.opBoolean","COPY",EDGE,{"derivedFrom":makeQuery(id+"F3.opExtrude","SWEPT_EDGE",EDGE,{"disambiguationData":[OSD([sQuery(id+"F0.wireOp",EDGE,"E5.MirrorCS"),sQuery(id+"F0.wireOp",EDGE,"E6.MirrorCS"),sQuery(id+"F2.wireOp",EDGE,"E16"),sQuery(id+"F2.wireOp",EDGE,"E46")])]})});
            var Q14;
            Q14=makeQuery(id+"F3.boolean.opBoolean","COPY",EDGE,{"derivedFrom":makeQuery(id+"F3.opExtrude","SWEPT_EDGE",EDGE,{"disambiguationData":[OSD([sQuery(id+"F2.wireOp",EDGE,"E15"),sQuery(id+"F2.wireOp",EDGE,"E17")])]})});
            var Q15;
            Q15=makeQuery(id+"F3.boolean.opBoolean","COPY",EDGE,{"derivedFrom":makeQuery(id+"F3.opExtrude","SWEPT_EDGE",EDGE,{"disambiguationData":[OSD([sQuery(id+"F2.wireOp",EDGE,"E21"),sQuery(id+"F2.wireOp",EDGE,"E45")])]})});
            var Q16;
            Q16=makeQuery(id+"F3.boolean.opBoolean","COPY",EDGE,{"derivedFrom":makeQuery(id+"F3.opExtrude","SWEPT_EDGE",EDGE,{"disambiguationData":[OSD([sQuery(id+"F2.wireOp",EDGE,"E47"),sQuery(id+"F2.wireOp",EDGE,"OQKDx2rC-8p01-W7AD-8jVz-H10RrjrdnyRq")])]})});
            var Q17;
            Q17=makeQuery(id+"F3.boolean.opBoolean","COPY",EDGE,{"derivedFrom":makeQuery(id+"F3.opExtrude","SWEPT_EDGE",EDGE,{"disambiguationData":[OSD([sQuery(id+"F2.wireOp",EDGE,"Vc8ZtUI0-CAgl-CdUB-t4W3-tU28hb1vTwv8"),sQuery(id+"F2.wireOp",EDGE,"kiQfGZOA-uULj-dTf1-FmXA-rcEVP8aInjXC")])]})});
            fillet(context, id + "F6", {"entities" : qUnion([Q0, Q1, Q2, Q3, Q4, Q5, Q6, Q7, Q8, Q9, Q10, Q11, Q12, Q13, Q14, Q15, Q16, Q17]), "radius" : 3 * mm, "tangentPropagation" : true, "allowEdgeOverflow" : false});
        }
        {
            var Q0;
            Q0=makeQuery(id+"F3.boolean.opBoolean","COPY",EDGE,{"derivedFrom":makeQuery(id+"F3.opExtrude","CAP_EDGE",EDGE,{"disambiguationData":[OSD([sQuery(id+"F2.wireOp",EDGE,"E18")])],"isStart":true})});
            var Q1;
            Q1=makeQuery(id+"F3.boolean.opBoolean","COPY",EDGE,{"derivedFrom":makeQuery(id+"F3.opExtrude","CAP_EDGE",EDGE,{"disambiguationData":[OSD([sQuery(id+"F2.wireOp",EDGE,"E15")])],"isStart":true})});
            var Q2;
            Q2=makeQuery(id+"F3.boolean.opBoolean","COPY",EDGE,{"derivedFrom":makeQuery(id+"F3.opExtrude","CAP_EDGE",EDGE,{"disambiguationData":[OSD([sQuery(id+"F2.wireOp",EDGE,"E16")])],"isStart":true})});
            var Q3;
            Q3=makeQuery(id+"F3.boolean.opBoolean","COPY",EDGE,{"derivedFrom":makeQuery(id+"F3.opExtrude","CAP_EDGE",EDGE,{"disambiguationData":[OSD([sQuery(id+"F2.wireOp",EDGE,"E44")])],"isStart":true})});
            var Q4;
            Q4=makeQuery(id+"F3.boolean.opBoolean","COPY",EDGE,{"derivedFrom":makeQuery(id+"F3.opExtrude","CAP_EDGE",EDGE,{"disambiguationData":[OSD([sQuery(id+"F2.wireOp",EDGE,"E36.3")])],"isStart":true})});
            var Q5;
            Q5=makeQuery(id+"F3.boolean.opBoolean","COPY",EDGE,{"derivedFrom":makeQuery(id+"F3.opExtrude","CAP_EDGE",EDGE,{"disambiguationData":[OSD([sQuery(id+"F2.wireOp",EDGE,"E36.4")])],"isStart":true})});
            var Q6;
            Q6=makeQuery(id+"F6.opFillet","BLEND_EDGE",EDGE,{"blendedFrom":[makeQuery(id+"F3.boolean.opBoolean","COPY",EDGE,{"derivedFrom":makeQuery(id+"F3.opExtrude","SWEPT_EDGE",EDGE,{"disambiguationData":[OSD([sQuery(id+"F2.wireOp",EDGE,"E25"),sQuery(id+"F2.wireOp",EDGE,"E36.5")])]})}),makeQuery(id+"F1.opExtrude","SWEPT_FACE",FACE,{"disambiguationData":[OSD([sQuery(id+"F0.wireOp",EDGE,"E4"),sQuery(id+"F0.wireOp",EDGE,"E6.MirrorCS")])]})],"blendedInto":[makeQuery(id+"F1.opExtrude","SWEPT_FACE",FACE,{"disambiguationData":[OSD([sQuery(id+"F0.wireOp",EDGE,"E4"),sQuery(id+"F0.wireOp",EDGE,"E6.MirrorCS")])]})]});
            var Q7;
            Q7=makeQuery(id+"F3.boolean.opBoolean","COPY",EDGE,{"derivedFrom":makeQuery(id+"F3.opExtrude","CAP_EDGE",EDGE,{"disambiguationData":[OSD([sQuery(id+"F2.wireOp",EDGE,"E53")])],"isStart":true})});
            var Q8;
            Q8=makeQuery(id+"F3.boolean.opBoolean","COPY",EDGE,{"derivedFrom":makeQuery(id+"F3.opExtrude","CAP_EDGE",EDGE,{"disambiguationData":[OSD([sQuery(id+"F2.wireOp",EDGE,"E90.trimOffspring")])],"isStart":true})});
            var Q9;
            Q9=makeQuery(id+"F3.boolean.opBoolean","COPY",EDGE,{"derivedFrom":makeQuery(id+"F3.opExtrude","CAP_EDGE",EDGE,{"disambiguationData":[OSD([sQuery(id+"F2.wireOp",EDGE,"E29")])],"isStart":true})});
            var Q10;
            Q10=makeQuery(id+"F6.opFillet","BLEND_EDGE",EDGE,{"blendedFrom":[makeQuery(id+"F3.boolean.opBoolean","COPY",EDGE,{"derivedFrom":makeQuery(id+"F3.opExtrude","SWEPT_EDGE",EDGE,{"disambiguationData":[OSD([sQuery(id+"F2.wireOp",EDGE,"E27"),sQuery(id+"F2.wireOp",EDGE,"E36.0")])]})}),makeQuery(id+"F1.opExtrude","SWEPT_FACE",FACE,{"disambiguationData":[OSD([sQuery(id+"F0.wireOp",EDGE,"E4"),sQuery(id+"F0.wireOp",EDGE,"E6.MirrorCS")])]})],"blendedInto":[makeQuery(id+"F1.opExtrude","SWEPT_FACE",FACE,{"disambiguationData":[OSD([sQuery(id+"F0.wireOp",EDGE,"E4"),sQuery(id+"F0.wireOp",EDGE,"E6.MirrorCS")])]})]});
            var Q11;
            Q11=makeQuery(id+"F3.boolean.opBoolean","COPY",EDGE,{"derivedFrom":makeQuery(id+"F3.opExtrude","CAP_EDGE",EDGE,{"disambiguationData":[OSD([sQuery(id+"F2.wireOp",EDGE,"E33")])],"isStart":true})});
            var Q12;
            Q12=makeQuery(id+"F3.boolean.opBoolean","COPY",EDGE,{"derivedFrom":makeQuery(id+"F3.opExtrude","CAP_EDGE",EDGE,{"disambiguationData":[OSD([sQuery(id+"F2.wireOp",EDGE,"E59")])],"isStart":true})});
            var Q13;
            Q13=makeQuery(id+"F3.boolean.opBoolean","COPY",EDGE,{"derivedFrom":makeQuery(id+"F3.opExtrude","CAP_EDGE",EDGE,{"disambiguationData":[OSD([sQuery(id+"F2.wireOp",EDGE,"E83.trimOffspring")])],"isStart":true})});
            var Q14;
            Q14=makeQuery(id+"F3.boolean.opBoolean","COPY",EDGE,{"derivedFrom":makeQuery(id+"F3.opExtrude","CAP_EDGE",EDGE,{"disambiguationData":[OSD([sQuery(id+"F2.wireOp",EDGE,"E89")])],"isStart":true})});
            var Q15;
            Q15=makeQuery(id+"F3.boolean.opBoolean","COPY",EDGE,{"derivedFrom":makeQuery(id+"F3.opExtrude","CAP_EDGE",EDGE,{"disambiguationData":[OSD([sQuery(id+"F2.wireOp",EDGE,"E87.trimOffspring")])],"isStart":true})});
            var Q16;
            Q16=makeQuery(id+"F3.boolean.opBoolean","COPY",EDGE,{"derivedFrom":makeQuery(id+"F3.opExtrude","CAP_EDGE",EDGE,{"disambiguationData":[OSD([sQuery(id+"F2.wireOp",EDGE,"E35")])],"isStart":true})});
            var Q17;
            Q17=makeQuery(id+"F3.boolean.opBoolean","INTERSECT",EDGE,{"derivedFrom":[makeQuery(id+"F1.opExtrude","SWEPT_FACE",FACE,{"disambiguationData":[OSD([sQuery(id+"F0.wireOp",EDGE,"E3"),sQuery(id+"F0.wireOp",EDGE,"E7.MirrorCS")])]}),makeQuery(id+"F3.opExtrude","SWEPT_FACE",FACE,{"disambiguationData":[OSD([sQuery(id+"F2.wireOp",EDGE,"E35")])]})]});
            var Q18;
            Q18=makeQuery(id+"F1.opExtrude","SWEPT_EDGE",EDGE,{"disambiguationData":[OSD([sQuery(id+"F0.wireOp",EDGE,"E5.MirrorCS"),sQuery(id+"F0.wireOp",EDGE,"E7.MirrorCS")])]});
            var Q19;
            Q19=makeQuery(id+"F3.boolean.opBoolean","INTERSECT",EDGE,{"derivedFrom":[makeQuery(id+"F1.opExtrude","SWEPT_FACE",FACE,{"disambiguationData":[OSD([sQuery(id+"F0.wireOp",EDGE,"E3"),sQuery(id+"F0.wireOp",EDGE,"E7.MirrorCS")])]}),makeQuery(id+"F3.opExtrude","SWEPT_FACE",FACE,{"disambiguationData":[OSD([sQuery(id+"F2.wireOp",EDGE,"E17")])]})]});
            var Q20;
            Q20=makeQuery(id+"F3.boolean.opBoolean","INTERSECT",EDGE,{"derivedFrom":[makeQuery(id+"F1.opExtrude","SWEPT_FACE",FACE,{"disambiguationData":[OSD([sQuery(id+"F0.wireOp",EDGE,"E3"),sQuery(id+"F0.wireOp",EDGE,"E7.MirrorCS")])]}),makeQuery(id+"F3.opExtrude","SWEPT_FACE",FACE,{"disambiguationData":[OSD([sQuery(id+"F2.wireOp",EDGE,"E41")])]})]});
            var Q21;
            Q21=makeQuery(id+"F3.boolean.opBoolean","INTERSECT",EDGE,{"derivedFrom":[makeQuery(id+"F1.opExtrude","SWEPT_FACE",FACE,{"disambiguationData":[OSD([sQuery(id+"F0.wireOp",EDGE,"E3"),sQuery(id+"F0.wireOp",EDGE,"E7.MirrorCS")])]}),makeQuery(id+"F3.opExtrude","SWEPT_FACE",FACE,{"disambiguationData":[OSD([sQuery(id+"F2.wireOp",EDGE,"E88.trimOffspring")])]})]});
            var Q22;
            Q22=makeQuery(id+"F1.opExtrude","SWEPT_FACE",FACE,{"disambiguationData":[OSD([sQuery(id+"F0.wireOp",EDGE,"E3"),sQuery(id+"F0.wireOp",EDGE,"E7.MirrorCS")])]});
            chamfer(context, id + "F7", {"entities" : qUnion([Q0, Q1, Q2, Q3, Q4, Q5, Q6, Q7, Q8, Q9, Q10, Q11, Q12, Q13, Q14, Q15, Q16, Q17, Q18, Q19, Q20, Q21, Q22]), "width" : 0.5 * mm, "tangentPropagation" : true});
        }
    });
